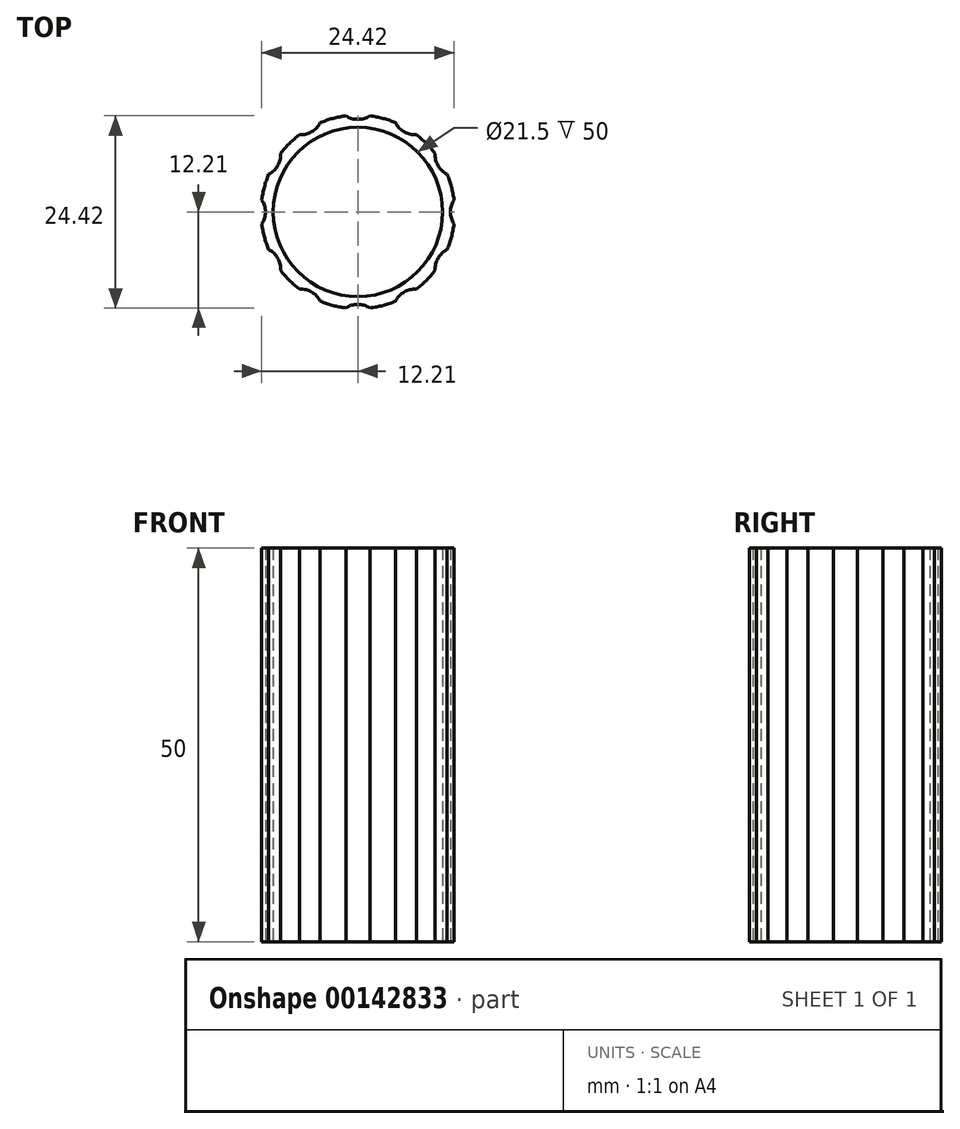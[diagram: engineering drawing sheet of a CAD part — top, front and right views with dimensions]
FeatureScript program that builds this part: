
annotation { "Feature Type Name" : "Feature", "Feature Type Description" : "" }
export const myFeature = defineFeature(function(context is Context, id is Id, definition is map)
    precondition{}
    {
        {
            var Q0;
            Q0=qCreatedBy(makeId("Top.planeOp"),FACE);
            var sketch = newSketch(context, id + "F0", { "sketchPlane" : qUnion([Q0])});
            skArc(sketch, "E0", {"start": v(-1.52, 12.2) * mm, "mid": v(-3.18, 11.88) * mm, "end": v(-4.79, 11.33) * mm});
            skCircle(sketch, "E1", {"center": v(0, 0) * mm, "radius": 10.75 * mm});
            skPoint(sketch, "E2.center.orphan", {"position": v(0, 14.5) * mm});
            skArc(sketch, "E3", {"start": v(-1.52, 12.2) * mm, "mid": v(0, 11.75) * mm, "end": v(1.52, 12.2) * mm});
            skArc(sketch, "E4.1.0", {"start": v(-7.42, 9.81) * mm, "mid": v(-5.88, 10.18) * mm, "end": v(-4.79, 11.33) * mm});
            skArc(sketch, "E4.2.0", {"start": v(-11.33, 4.79) * mm, "mid": v(-10.18, 5.88) * mm, "end": v(-9.81, 7.42) * mm});
            skArc(sketch, "E4.3.0", {"start": v(-12.2, -1.52) * mm, "mid": v(-11.75, 0) * mm, "end": v(-12.2, 1.52) * mm});
            skArc(sketch, "E4.4.0", {"start": v(-9.81, -7.42) * mm, "mid": v(-10.18, -5.87) * mm, "end": v(-11.33, -4.79) * mm});
            skArc(sketch, "E4.5.0", {"start": v(-4.79, -11.33) * mm, "mid": v(-5.87, -10.18) * mm, "end": v(-7.42, -9.81) * mm});
            skArc(sketch, "E4.6.0", {"start": v(1.52, -12.2) * mm, "mid": v(0, -11.75) * mm, "end": v(-1.52, -12.2) * mm});
            skArc(sketch, "E4.7.0", {"start": v(7.42, -9.81) * mm, "mid": v(5.87, -10.18) * mm, "end": v(4.79, -11.33) * mm});
            skArc(sketch, "E4.8.0", {"start": v(11.33, -4.79) * mm, "mid": v(10.18, -5.88) * mm, "end": v(9.81, -7.42) * mm});
            skArc(sketch, "E4.9.0", {"start": v(12.2, 1.52) * mm, "mid": v(11.75, 0) * mm, "end": v(12.2, -1.52) * mm});
            skArc(sketch, "E4.10.0", {"start": v(9.81, 7.42) * mm, "mid": v(10.18, 5.88) * mm, "end": v(11.33, 4.79) * mm});
            skArc(sketch, "E4.11.0", {"start": v(4.79, 11.33) * mm, "mid": v(5.88, 10.18) * mm, "end": v(7.42, 9.81) * mm});
            skArc(sketch, "E5.trimOffspring", {"start": v(-7.42, 9.81) * mm, "mid": v(-8.7, 8.7) * mm, "end": v(-9.81, 7.42) * mm});
            skArc(sketch, "E6.trimOffspring", {"start": v(-11.33, 4.79) * mm, "mid": v(-11.88, 3.18) * mm, "end": v(-12.2, 1.52) * mm});
            skArc(sketch, "E7.trimOffspring", {"start": v(-12.2, -1.52) * mm, "mid": v(-11.88, -3.18) * mm, "end": v(-11.33, -4.79) * mm});
            skArc(sketch, "E8.trimOffspring", {"start": v(-9.81, -7.42) * mm, "mid": v(-8.7, -8.7) * mm, "end": v(-7.42, -9.81) * mm});
            skArc(sketch, "E9.trimOffspring", {"start": v(-4.79, -11.33) * mm, "mid": v(-3.18, -11.88) * mm, "end": v(-1.52, -12.2) * mm});
            skArc(sketch, "E10.trimOffspring", {"start": v(1.52, -12.2) * mm, "mid": v(3.18, -11.88) * mm, "end": v(4.79, -11.33) * mm});
            skArc(sketch, "E11.trimOffspring", {"start": v(7.42, -9.81) * mm, "mid": v(8.7, -8.7) * mm, "end": v(9.81, -7.42) * mm});
            skArc(sketch, "E12.trimOffspring", {"start": v(11.33, -4.79) * mm, "mid": v(11.88, -3.18) * mm, "end": v(12.2, -1.52) * mm});
            skArc(sketch, "E13.trimOffspring", {"start": v(12.2, 1.52) * mm, "mid": v(11.88, 3.18) * mm, "end": v(11.33, 4.79) * mm});
            skArc(sketch, "E14.trimOffspring", {"start": v(9.81, 7.42) * mm, "mid": v(8.7, 8.7) * mm, "end": v(7.42, 9.81) * mm});
            skArc(sketch, "E15.trimOffspring", {"start": v(4.79, 11.33) * mm, "mid": v(3.18, 11.88) * mm, "end": v(1.52, 12.2) * mm});
            skSolve(sketch);
        }
        {
            var Q0;
            Q0 = qSketchRegion(id + "F0", true);
            extrude(context, id + "F1", {"entities" : qUnion([Q0]), "depth" : 50 * mm});
        }
    });
